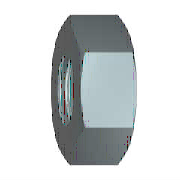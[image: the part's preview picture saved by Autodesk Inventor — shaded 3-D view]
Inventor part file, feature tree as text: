
AUTODESK INVENTOR PART (.ipt)
format: ipt  version: 2025 (Build 290162010, 162A)  size: 162,816 bytes
history: native  units: mm (DEFAULTED — no unit token found)
features: chamfer x1, hole x1, other x1, plane x1
ambient origin geometry x7: Origin, YZ Plane, XZ Plane, X Axis, Y Axis, Z Axis, Center Point
bodies: Solid1 (feature_tree), Body (feature_tree)
feature tree (4):
  chamfer  "Chamfer1"  Distance=18.475209mm
  hole  "Thread"  [1 undecoded]
  other  "Work Axis1"
  plane  "Work Plane1"
note: 1 required parameter value undecoded (feature->parameter linkage not recoverable at this tier; creation-order binding heuristic only, values carry confidence <= 0.55)
